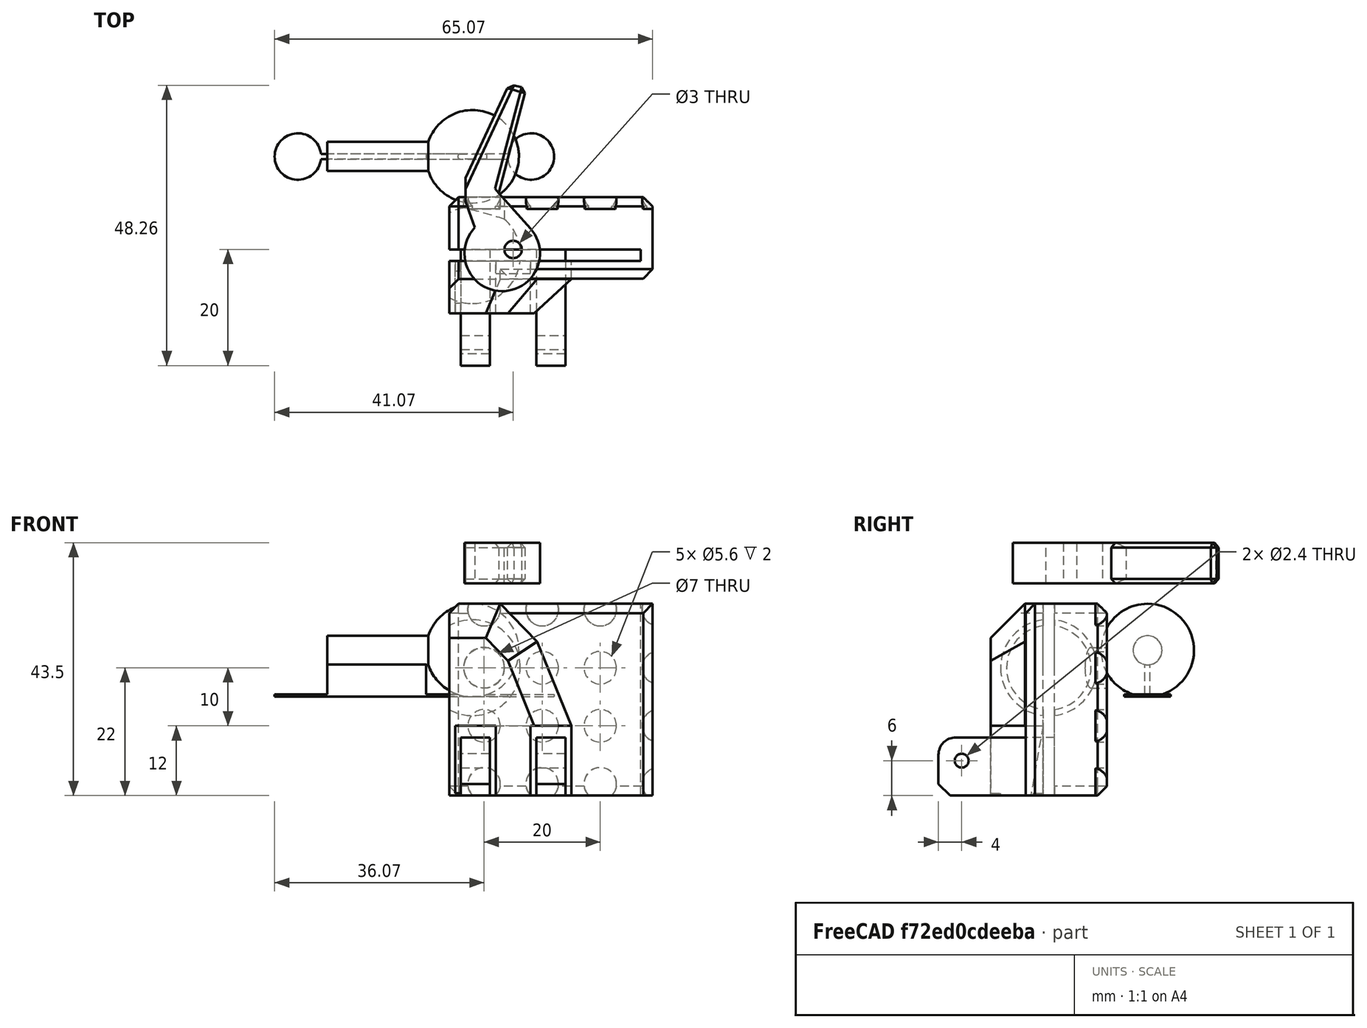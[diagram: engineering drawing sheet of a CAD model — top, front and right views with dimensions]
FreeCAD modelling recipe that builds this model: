
FCSTD DOCUMENT  (FreeCAD 0.18R4 (GitTag))
Label: Ballsocket
License: All rights reserved
LicenseURL: http://en.wikipedia.org/wiki/All_rights_reserved
objects: Sketcher::SketchObject×15, PartDesign::Pocket×7, PartDesign::Pad×4, PartDesign::Chamfer×4, Part::FeaturePython×4, Mesh::Feature×3, Part::Sphere×2, PartDesign::Body×2, Part::MultiFuse×2, PartDesign::Fillet×1, Part::Cylinder×1, Part::Box×1, PartDesign::LinearPattern×1, Part::Extrusion×1, Part::Cut×1, App::DocumentObjectGroup×1
note: 57 computed .brp shape members not serialized (recipe doc carries the construction recipe); baked Part::Feature solids carry a one-line shape summary decoded from their .brp

FEATURE [Sketcher::SketchObject] Sketch
  MapMode = 5
  Support = -> [XY_Plane]
  sketch-geometry (4):
    g0: LineSegment StartX=-22 StartY=18 StartZ=0 EndX=13 EndY=18 EndZ=0
    g1: LineSegment StartX=13 StartY=18 StartZ=0 EndX=13 EndY=-15 EndZ=0
    g2: LineSegment StartX=13 StartY=-15 StartZ=0 EndX=-22 EndY=-15 EndZ=0
    g3: LineSegment StartX=-22 StartY=-15 StartZ=0 EndX=-22 EndY=18 EndZ=0
  constraints (12):
    c: Coincident(g0,g1)
    c: Coincident(g1,g2)
    c: Coincident(g2,g3)
    c: Coincident(g3,g0)
    c: Horizontal(g2)
    c: Vertical(g1)
    c: DistanceX(g2) = -22
    c: DistanceY(g2) = -15
    c: Horizontal(g0)
    c: DistanceX(g0) = 13
    c: Vertical(g3)
    c: DistanceY(g0) = 18
FEATURE [PartDesign::Pad] Pad
  Length = 20
  Length2 = 100
  Profile = -> Sketch
  Refine = true
  Type = 0
FEATURE [Sketcher::SketchObject] Sketch001
  MapMode = 5
  Placement = pos=(0,0,20) rot=(0,0,1;0rad)
  Support = -> [Pad]
  sketch-geometry (8):
    g0: LineSegment StartX=-21 StartY=-3 StartZ=0 EndX=-14 EndY=-3 EndZ=0
    g1: LineSegment StartX=-14 StartY=-3 StartZ=0 EndX=-14 EndY=-15 EndZ=0
    g2: LineSegment StartX=-14 StartY=-15 StartZ=0 EndX=-21 EndY=-15 EndZ=0
    g3: LineSegment StartX=-21 StartY=-15 StartZ=0 EndX=-21 EndY=-3 EndZ=0
    g4: LineSegment StartX=-8 StartY=-3 StartZ=0 EndX=-1 EndY=-3 EndZ=0
    g5: LineSegment StartX=-1 StartY=-3 StartZ=0 EndX=-1 EndY=-15 EndZ=0
    g6: LineSegment StartX=-1 StartY=-15 StartZ=0 EndX=-8 EndY=-15 EndZ=0
    g7: LineSegment StartX=-8 StartY=-15 StartZ=0 EndX=-8 EndY=-3 EndZ=0
  constraints (24):
    c: Coincident(g0,g1)
    c: Coincident(g1,g2)
    c: Coincident(g2,g3)
    c: Coincident(g3,g0)
    c: Horizontal(g0)
    c: Horizontal(g2)
    c: Vertical(g1)
    c: Coincident(g4,g5)
    c: Coincident(g5,g6)
    c: Coincident(g6,g7)
    c: Coincident(g7,g4)
    c: Horizontal(g4)
    c: Horizontal(g6)
    c: Vertical(g5)
    c: Equal(g7,g3)
    c: DistanceX(g0) = -21
    c: DistanceX(g0,g0) = 7
    c: DistanceX(g0,g4) = 6
    c: Distance(g1) = 12
    c: Horizontal(g0,g4)
    c: Vertical(g3)
    c: Vertical(g7)
    c: DistanceY(g2) = -15
    c: DistanceX(g4,g4) = 7
FEATURE [PartDesign::Pocket] Pocket
  BaseFeature = -> Pad
  Length = 10
  Length2 = 100
  Profile = -> Sketch001
  Refine = true
  Type = 0
FEATURE [Sketcher::SketchObject] Sketch003
  MapMode = 5
  Placement = pos=(0,0,0) rot=(0.57735,0.57735,0.57735;2.0944rad)
  Support = -> [YZ_Plane]
  sketch-geometry (1):
    g0: Circle CenterX=-9 CenterY=25 CenterZ=0 NormalX=0 NormalY=0 NormalZ=1 AngleXU=0 Radius=1.2
  constraints (3):
    c: DistanceY(g0) = 25
    c: Radius(g0) = 1.2
    c: DistanceX(g0) = -9
FEATURE [Sketcher::SketchObject] Sketch004
  MapMode = 5
  Placement = pos=(0,0,0) rot=(1,0,0;1.5708rad)
  Support = -> [XZ_Plane]
  sketch-geometry (4):
    g0: LineSegment StartX=-25 StartY=11 StartZ=0 EndX=11 EndY=11 EndZ=0
    g1: LineSegment StartX=11 StartY=11 StartZ=0 EndX=11 EndY=9 EndZ=0
    g2: LineSegment StartX=11 StartY=9 StartZ=0 EndX=-25 EndY=9 EndZ=0
    g3: LineSegment StartX=-25 StartY=9 StartZ=0 EndX=-25 EndY=11 EndZ=0
  constraints (12):
    c: Coincident(g0,g1)
    c: Coincident(g1,g2)
    c: Coincident(g2,g3)
    c: Coincident(g3,g0)
    c: Horizontal(g0)
    c: Horizontal(g2)
    c: Vertical(g1)
    c: Vertical(g3)
    c: DistanceX(g0) = 11
    c: DistanceX(g0) = -25
    c: DistanceY(g2) = 9
    c: DistanceY(g0) = 11
FEATURE [PartDesign::Pocket] Pocket002
  BaseFeature = -> Pocket
  Length = 5
  Length2 = 100
  Midplane = true
  Profile = -> Sketch004
  Refine = true
  Type = 1
FEATURE [Sketcher::SketchObject] Sketch002
  MapMode = 5
  Placement = pos=(0,-2e-15,9) rot=(0,0,1;0rad)
  Support = -> [Pocket002]
  sketch-geometry (8):
    g0: LineSegment StartX=-20 StartY=-5 StartZ=0 EndX=-15 EndY=-5 EndZ=0
    g1: LineSegment StartX=-15 StartY=-5 StartZ=0 EndX=-15 EndY=-15 EndZ=0
    g2: LineSegment StartX=-15 StartY=-15 StartZ=0 EndX=-20 EndY=-15 EndZ=0
    g3: LineSegment StartX=-20 StartY=-15 StartZ=0 EndX=-20 EndY=-5 EndZ=0
    g4: LineSegment StartX=-7 StartY=-5 StartZ=0 EndX=-2 EndY=-5 EndZ=0
    g5: LineSegment StartX=-2 StartY=-5 StartZ=0 EndX=-2 EndY=-15 EndZ=0
    g6: LineSegment StartX=-2 StartY=-15 StartZ=0 EndX=-7 EndY=-15 EndZ=0
    g7: LineSegment StartX=-7 StartY=-15 StartZ=0 EndX=-7 EndY=-5 EndZ=0
  constraints (24):
    c: Coincident(g0,g1)
    c: Coincident(g1,g2)
    c: Coincident(g2,g3)
    c: Coincident(g3,g0)
    c: Horizontal(g0)
    c: Horizontal(g2)
    c: Vertical(g1)
    c: Coincident(g4,g5)
    c: Coincident(g5,g6)
    c: Coincident(g6,g7)
    c: Coincident(g7,g4)
    c: Horizontal(g4)
    c: Horizontal(g6)
    c: Vertical(g5)
    c: DistanceX(g0) = -20
    c: DistanceX(g0,g0) = 5
    c: DistanceX(g0,g4) = 8
    c: Equal(g0,g4)
    c: Equal(g7,g3)
    c: Distance(g3) = 10
    c: Vertical(g3)
    c: Vertical(g7)
    c: Horizontal(g4,g0)
    c: DistanceY(g2) = -15
FEATURE [PartDesign::Pad] Pad001
  BaseFeature = -> Pocket002
  Length = 20
  Length2 = 100
  Profile = -> Sketch002
  Refine = true
  Type = 0
FEATURE [PartDesign::Pocket] Pocket001
  BaseFeature = -> Pad001
  Length = 5
  Length2 = 100
  Profile = -> Sketch003
  Refine = true
  Type = 1
FEATURE [Part::Sphere] Sphere
  Angle1 = -90
  Angle2 = 90
  Angle3 = 360
  AttacherType = Attacher::AttachEngine3D
  Placement = pos=(-18,7,10) rot=(0,0,1;0rad)
  Radius = 8.3
FEATURE [Sketcher::SketchObject] Sketch005
  MapMode = 5
  Placement = pos=(0,0,20) rot=(0,0,1;0rad)
  Support = -> [Pocket001]
  sketch-geometry (7):
    g0: LineSegment StartX=-6.87841 StartY=11.5067 StartZ=0 EndX=-1 EndY=-3 EndZ=0
    g1: LineSegment StartX=-1 StartY=-3 StartZ=0 EndX=-1 EndY=-16.5217 EndZ=0
    g2: LineSegment StartX=-1 StartY=-16.5217 StartZ=0 EndX=16.1456 EndY=-16.5217 EndZ=0
    g3: LineSegment StartX=16.1456 StartY=-16.5217 StartZ=0 EndX=16.1456 EndY=20.3335 EndZ=0
    g4: LineSegment StartX=-13.2042 StartY=18 StartZ=0 EndX=-18.5565 EndY=20.3335 EndZ=0
    g5: LineSegment StartX=-18.5565 StartY=20.3335 StartZ=0 EndX=16.1456 EndY=20.3335 EndZ=0
    g6: LineSegment StartX=-13.2042 StartY=18 StartZ=0 EndX=-6.87841 EndY=11.5067 EndZ=0
  constraints (17):
    c: Vertical(g1)
    c: Coincident(g1,g2)
    c: Horizontal(g2)
    c: Coincident(g2,g3)
    c: Vertical(g3)
    c: Coincident(g5,g4)
    c: Coincident(g5,g3)
    c: Horizontal(g5)
    c: Coincident(g0,g1)
    c: DistanceX(g0) = -1
    c: DistanceY(g0) = -3
    c: DistanceX(g0) = -6.87841
    c: DistanceY(g0) = 11.5067
    c: DistanceX(g4) = -13.2042
    c: DistanceY(g4) = 18
    c: Coincident(g6,g4)
    c: Coincident(g6,g0)
FEATURE [PartDesign::Pocket] Pocket003
  BaseFeature = -> Pocket001
  Length = 6
  Length2 = 100
  Profile = -> Sketch005
  Refine = true
  Type = 0
FEATURE [PartDesign::Chamfer] Chamfer
  Base = -> Pocket003 [Edge5,Edge21,Edge29]
  BaseFeature = -> Pocket003
  Size = 5.9
FEATURE [Sketcher::SketchObject] Sketch006
  ExternalGeometry = -> [Chamfer]
  MapMode = 5
  Placement = pos=(0,0,20) rot=(0,0,1;0rad)
  Support = -> [Chamfer]
FEATURE [PartDesign::Chamfer] Chamfer001
  Base = -> Chamfer [Face8,Edge9,Edge41,Edge4,Edge24,Edge17,Edge3]
  BaseFeature = -> Chamfer
  Size = 1.6
FEATURE [PartDesign::Chamfer] Chamfer002
  Base = -> Chamfer001 [Edge78,Edge83]
  BaseFeature = -> Chamfer001
  Size = 2
FEATURE [PartDesign::Fillet] Fillet
  Base = -> Chamfer002 [Edge87,Edge75]
  BaseFeature = -> Chamfer002
  Radius = 3
FEATURE [Sketcher::SketchObject] Sketch007
  MapMode = 5
  Placement = pos=(0,0,0) rot=(0.57735,0.57735,0.57735;2.0944rad)
  Support = -> [YZ_Plane001]
  sketch-geometry (11):
    g0: ArcOfCircle CenterX=-0.68404 CenterY=-1.87939 CenterZ=0 NormalX=0 NormalY=0 NormalZ=1 AngleXU=0 Radius=6.5 StartAngle=0.843713 EndAngle=5.47308
    g1: LineSegment [constr] StartX=0 StartY=0 StartZ=0 EndX=-0.68404 EndY=-1.87939 EndZ=0
    g2: LineSegment StartX=3.79722 StartY=-6.58771 StartZ=0 EndX=8.22696 EndY=-8.2 EndZ=0
    g3: LineSegment StartX=8.22696 StartY=-8.2 StartZ=0 EndX=12.3057 EndY=-8.2 EndZ=0
    g4: LineSegment StartX=12.3057 StartY=-8.2 StartZ=0 EndX=28.4613 EndY=-0.655032 EndZ=0
    g5: LineSegment StartX=3.63647 StartY=2.97687 StartZ=0 EndX=9.73628 EndY=-2.45001 EndZ=0
    g6: LineSegment StartX=9.73628 StartY=-2.45001 StartZ=0 EndX=27.7024 EndY=2.2474 EndZ=0
    g7: LineSegment StartX=27.7024 StartY=2.2474 StartZ=0 EndX=28.4613 EndY=-0.655032 EndZ=0
    g8: Circle CenterX=0 CenterY=0 CenterZ=0 NormalX=0 NormalY=0 NormalZ=1 AngleXU=0 Radius=1.5
    g9: LineSegment [constr] StartX=3.08498 StartY=3.46752 StartZ=0 EndX=0.99704 EndY=1.12067 EndZ=0
    g10: LineSegment [constr] StartX=-0.68404 StartY=-8.37939 StartZ=0 EndX=-0.68404 EndY=-12.1798 EndZ=0
  constraints (28):
    c: Coincident(g1,g-1)
    c: Coincident(g1,g0)
    c: Distance(g1) = 2
    c: Radius(g0) = 6.5
    c: Coincident(g2,g0)
    c: Perpendicular(g1,g2)
    c: Coincident(g2,g3)
    c: Horizontal(g3)
    c: Coincident(g3,g4)
    c: Tangent(g0,g5) = 1.5708
    c: Coincident(g6,g5)
    c: Coincident(g7,g6)
    c: Coincident(g7,g4)
    c: Perpendicular(g7,g6)
    c: Distance(g7) = 3
    c: Coincident(g8,g-1)
    c: Radius(g8) = 1.5
    c: PointOnObject(g9,g5)
    c: PointOnObject(g9,g8)
    c: Distance(g9) = 3.1412
    c: Perpendicular(g5,g9)
    c: Perpendicular(g8,g9)
    c: Angle(g1) = -1.91986
    c: DistanceY(g2) = -8.2
    c: PointOnObject(g10,g0)
    c: Vertical(g10)
    c: Perpendicular(g0,g10)
    c: DistanceY(g10) = -8.37939
FEATURE [PartDesign::Pad] Pad002
  Length = 7
  Length2 = 100
  Midplane = true
  Placement = pos=(0,0,0) rot=(0.57735,0.57735,0.57735;2.0944rad)
  Profile = -> Sketch007
  Refine = true
  Type = 0
FEATURE [PartDesign::Chamfer] Chamfer003
  Base = -> Pad002 [Edge18,Edge12,Edge19,Edge13,Face5]
  BaseFeature = -> Pad002
  Placement = pos=(0,0,0) rot=(0.57735,0.57735,0.57735;2.0944rad)
  Size = 0.8
FEATURE [PartDesign::Body] Body001  label="Lever"
  Group = -> [Sketch007,Pad002,Chamfer003]
  Origin = -> Origin001
  Placement = pos=(-11,-9,25) rot=(0,0,1;0rad)
  Tip = -> Chamfer003
FEATURE [Part::Sphere] Sphere001
  Angle1 = -90
  Angle2 = 90
  Angle3 = 360
  AttacherType = Attacher::AttachEngine3D
  Placement = pos=(-18,7,10) rot=(0,0,1;0rad)
  Radius = 8
FEATURE [Part::Cylinder] Cylinder
  Angle = 360
  AttacherType = Attacher::AttachEngine3D
  Height = 25
  Placement = pos=(-18,7,10) rot=(0,-1,0;1.5708rad)
  Radius = 2.5
FEATURE [Part::Box] Box  label="Cube"
  AttacherType = Attacher::AttachEngine3D
  Height = 8
  Length = 17
  Placement = pos=(-43,6.55,2) rot=(0,0,1;0rad)
  Width = 0.9
FEATURE [Part::MultiFuse] Fusion  label="Ball_withoutsupport"
  Refine = true
  Shapes = -> [Sphere001,Cylinder,Box]
FEATURE [Sketcher::SketchObject] Sketch008
  MapMode = 5
  Placement = pos=(0,0,20) rot=(0,0,1;0rad)
  Support = -> [Pad]
  sketch-geometry (2):
    g0: Circle CenterX=4 CenterY=7 CenterZ=0 NormalX=0 NormalY=0 NormalZ=1 AngleXU=0 Radius=3.3
    g1: Circle [constr] CenterX=4 CenterY=7 CenterZ=0 NormalX=0 NormalY=0 NormalZ=1 AngleXU=0 Radius=6.5
  constraints (5):
    c: DistanceY(g0) = 7
    c: Radius(g0) = 3.3
    c: Coincident(g1,g0)
    c: Radius(g1) = 6.5
    c: DistanceX(g0) = 4
FEATURE [Sketcher::SketchObject] Sketch009
  MapMode = 5
  Placement = pos=(0,0,14) rot=(0,0,1;0rad)
  Support = -> [Pocket003]
  expr: Constraints[4] = Sketch008.Constraints[4]
  expr: Constraints[3] = Sketch008.Constraints[3]
  expr: Constraints[1] = Sketch008.Constraints[1]
  expr: Constraints[0] = Sketch008.Constraints[0]
  sketch-geometry (2):
    g0: Circle [constr] CenterX=4 CenterY=7 CenterZ=0 NormalX=0 NormalY=0 NormalZ=1 AngleXU=0 Radius=3.3
    g1: Circle CenterX=4 CenterY=7 CenterZ=0 NormalX=0 NormalY=0 NormalZ=1 AngleXU=0 Radius=6.5
  constraints (5):
    c: DistanceY(g0) = 7
    c: Radius(g0) = 3.3
    c: Coincident(g1,g0)
    c: Radius(g1) = 6.5
    c: DistanceX(g0) = 4
FEATURE [Sketcher::SketchObject] Sketch010
  MapMode = 5
  Support = -> [XY_Plane]
  expr: Constraints[4] = Sketch008.Constraints[4]
  expr: Constraints[3] = Sketch008.Constraints[3]
  expr: Constraints[1] = Sketch008.Constraints[1]
  expr: Constraints[0] = Sketch008.Constraints[0]
  sketch-geometry (11):
    g0: Circle [constr] CenterX=4 CenterY=7 CenterZ=0 NormalX=0 NormalY=0 NormalZ=1 AngleXU=0 Radius=3.3
    g1: Circle [constr] CenterX=4 CenterY=7 CenterZ=0 NormalX=0 NormalY=0 NormalZ=1 AngleXU=0 Radius=6.5
    g2: Circle CenterX=14 CenterY=-13 CenterZ=0 NormalX=0 NormalY=0 NormalZ=1 AngleXU=0 Radius=2.8
    g3: Circle CenterX=4 CenterY=-13 CenterZ=0 NormalX=0 NormalY=0 NormalZ=1 AngleXU=0 Radius=2.8
    g4: Circle CenterX=-6 CenterY=-13 CenterZ=0 NormalX=0 NormalY=0 NormalZ=1 AngleXU=0 Radius=2.8
    g5: Circle CenterX=-16 CenterY=-13 CenterZ=0 NormalX=0 NormalY=0 NormalZ=1 AngleXU=0 Radius=2.8
    g6: Circle [constr] CenterX=-26 CenterY=-13 CenterZ=0 NormalX=0 NormalY=0 NormalZ=1 AngleXU=0 Radius=2.8
    g7: LineSegment [constr] StartX=14 StartY=-13 StartZ=0 EndX=4 EndY=-13 EndZ=0
    g8: LineSegment [constr] StartX=-6 StartY=-13 StartZ=0 EndX=4 EndY=-13 EndZ=0
    g9: LineSegment [constr] StartX=-6 StartY=-13 StartZ=0 EndX=-16 EndY=-13 EndZ=0
    g10: LineSegment [constr] StartX=-16 StartY=-13 StartZ=0 EndX=-26 EndY=-13 EndZ=0
  constraints (28):
    c: DistanceY(g0) = 7
    c: Radius(g0) = 3.3
    c: Coincident(g1,g0)
    c: Radius(g1) = 6.5
    c: DistanceX(g0) = 4
    c: DistanceY(g2,g0) = 20
    c: Coincident(g7,g2)
    c: Coincident(g7,g3)
    c: Coincident(g8,g4)
    c: Coincident(g8,g3)
    c: Coincident(g9,g4)
    c: Coincident(g9,g5)
    c: Horizontal(g9)
    c: Coincident(g10,g5)
    c: Coincident(g10,g6)
    c: Horizontal(g10)
    c: Horizontal(g8)
    c: Horizontal(g7)
    c: Equal(g7,g8)
    c: Equal(g8,g9)
    c: Equal(g9,g10)
    c: Vertical(g3,g0)
    c: Distance(g7) = 10
    c: Equal(g2,g3)
    c: Equal(g3,g4)
    c: Equal(g4,g5)
    c: Equal(g5,g6)
    c: Radius(g3) = 2.8
FEATURE [PartDesign::Pocket] Pocket006
  BaseFeature = -> Fillet
  Length = 2
  Length2 = 100
  Profile = -> Sketch010
  Refine = true
  Reversed = true
  Type = 0
FEATURE [PartDesign::LinearPattern] LinearPattern
  BaseFeature = -> Pocket006
  Direction = -> Sketch010 [V_Axis]
  Length = 30
  Occurrences = 4
  Originals = -> [Pocket006]
  Refine = true
FEATURE [Sketcher::SketchObject] Sketch011
  MapMode = 5
  Placement = pos=(0,0,2) rot=(1,0,0;3.14159rad)
  Support = -> [Fusion]
  sketch-geometry (6):
    g0: LineSegment StartX=-44.0943 StartY=-6.55 StartZ=0 EndX=-11.9024 EndY=-6.55 EndZ=0
    g1: LineSegment [constr] StartX=-11.9024 StartY=-6.55 StartZ=0 EndX=-11.9024 EndY=-7.45 EndZ=0
    g2: LineSegment StartX=-11.9024 StartY=-7.45 StartZ=0 EndX=-44.0943 EndY=-7.45 EndZ=0
    g3: LineSegment [constr] StartX=-44.0943 StartY=-7.45 StartZ=0 EndX=-44.0943 EndY=-6.55 EndZ=0
    g4: ArcOfCircle CenterX=-7.92778 CenterY=-7 CenterZ=0 NormalX=0 NormalY=0 NormalZ=1 AngleXU=0 Radius=4 StartAngle=3.25433 EndAngle=9.31204
    g5: ArcOfCircle CenterX=-48.0689 CenterY=-7 CenterZ=0 NormalX=0 NormalY=0 NormalZ=1 AngleXU=0 Radius=4 StartAngle=0.112739 EndAngle=6.17045
  constraints (16):
    c: Coincident(g0,g1)
    c: Coincident(g1,g2)
    c: Coincident(g2,g3)
    c: Coincident(g3,g0)
    c: Horizontal(g0)
    c: Horizontal(g2)
    c: Vertical(g1)
    c: Vertical(g3)
    c: Distance(g3) = 0.9
    c: DistanceY(g0) = -6.55
    c: Coincident(g4,g0)
    c: Coincident(g4,g2)
    c: Radius(g4) = 4
    c: Coincident(g5,g0)
    c: Coincident(g5,g2)
    c: Radius(g5) = 4
FEATURE [Part::Extrusion] Extrude
  Base = -> Sketch011
  Dir = (0,0,-1)
  DirMode = 2
  FaceMakerClass = Part::FaceMakerBullseye
  LengthFwd = 0.4
  LengthRev = 0
  Reversed = true
  Solid = true
  Symmetric = false
FEATURE [Part::MultiFuse] Fusion001  label="Ball"
  Refine = true
  Shapes = -> [Fusion,Extrude]
FEATURE [Sketcher::SketchObject] Sketch012
  MapMode = 5
  Placement = pos=(0,0,0) rot=(1,0,0;3.14159rad)
  Support = -> [Pad]
  sketch-geometry (1):
    g0: Circle CenterX=-16 CenterY=-7 CenterZ=0 NormalX=0 NormalY=0 NormalZ=1 AngleXU=0 Radius=3.5
  constraints (3):
    c: DistanceX(g0) = -16
    c: DistanceY(g0) = -7
    c: Radius(g0) = 3.5
FEATURE [PartDesign::Pocket] Pocket007
  BaseFeature = -> LinearPattern
  Length = 8
  Length2 = 100
  Profile = -> Sketch012
  Refine = true
  Type = 0
FEATURE [Sketcher::SketchObject] Sketch013
  MapMode = 5
  Placement = pos=(0,-15,0) rot=(1,0,0;1.5708rad)
  Support = -> [Pad]
  sketch-geometry (8):
    g0: LineSegment StartX=-21.5877 StartY=20 StartZ=0 EndX=-18.0644 EndY=20 EndZ=0
    g1: LineSegment StartX=-18.0644 StartY=20 StartZ=0 EndX=-18.0644 EndY=18.3 EndZ=0
    g2: LineSegment StartX=-18.0644 StartY=18.3 StartZ=0 EndX=-21.5877 EndY=18.3 EndZ=0
    g3: LineSegment StartX=-21.5877 StartY=18.3 StartZ=0 EndX=-21.5877 EndY=20 EndZ=0
    g4: LineSegment StartX=-21.4003 StartY=12.7 StartZ=0 EndX=-17.5021 EndY=12.7 EndZ=0
    g5: LineSegment StartX=-17.5021 StartY=12.7 StartZ=0 EndX=-17.5021 EndY=11 EndZ=0
    g6: LineSegment StartX=-17.5021 StartY=11 StartZ=0 EndX=-21.4003 EndY=11 EndZ=0
    g7: LineSegment StartX=-21.4003 StartY=11 StartZ=0 EndX=-21.4003 EndY=12.7 EndZ=0
  constraints (20):
    c: Coincident(g0,g1)
    c: Coincident(g1,g2)
    c: Coincident(g2,g3)
    c: Coincident(g3,g0)
    c: Horizontal(g0)
    c: Horizontal(g2)
    c: Vertical(g1)
    c: Vertical(g3)
    c: DistanceY(g0) = 20
    c: Distance(g3) = 1.7
    c: Coincident(g4,g5)
    c: Coincident(g5,g6)
    c: Coincident(g6,g7)
    c: Coincident(g7,g4)
    c: Horizontal(g4)
    c: Horizontal(g6)
    c: Vertical(g5)
    c: Vertical(g7)
    c: DistanceY(g6) = 11
    c: Equal(g7,g3)
FEATURE [PartDesign::Pad] Pad003
  BaseFeature = -> Pocket007
  Length = 0.4
  Length2 = 100
  Profile = -> Sketch013
  Refine = true
  Reversed = true
  Type = 0
FEATURE [Sketcher::SketchObject] Sketch014
  MapMode = 5
  Placement = pos=(-14,0,0) rot=(0.57735,-0.57735,-0.57735;2.0944rad)
  Support = -> [Pocket]
  sketch-geometry (3):
    g0: LineSegment StartX=3 StartY=11 StartZ=0 EndX=23 EndY=14.5265 EndZ=0
    g1: LineSegment StartX=3 StartY=11 StartZ=0 EndX=23 EndY=11 EndZ=0
    g2: LineSegment StartX=23 StartY=11 StartZ=0 EndX=23 EndY=14.5265 EndZ=0
  constraints (9):
    c: DistanceX(g0) = 3
    c: DistanceY(g0) = 11
    c: Angle(g0) = 0.174533
    c: Coincident(g0,g1)
    c: Horizontal(g1)
    c: Coincident(g1,g2)
    c: Vertical(g2)
    c: DistanceX(g1,g1) = 20
    c: Coincident(g0,g2)
FEATURE [PartDesign::Pocket] Pocket008
  BaseFeature = -> Pad003
  Length = 6
  Length2 = 100
  Profile = -> Sketch014
  Refine = true
  Type = 0
FEATURE [PartDesign::Body] Body  label="Socketbody"
  Group = -> [Sketch,Pad,Sketch001,Pocket,Pocket002,Sketch002,Pad001,Sketch003,Pocket001,Sketch004,Sketch005,Pocket003,Chamfer,Sketch006,Chamfer001,Chamfer002,Fillet,Pocket006,LinearPattern,Pocket007,Sketch012,Sketch008,Sketch009,Sketch010,Sketch013,Pad003,Sketch014,Pocket008]
  Origin = -> Origin
  Tip = -> Pocket008
FEATURE [Part::FeaturePython] Clone  label="Socketbody001"  # Draft clone (typed FeaturePython)
  AttacherType = Attacher::AttachEngine3D
  Fuse = false
  Objects = -> [Body]
  Scale = (1,1,1)
FEATURE [Part::Cut] Cut  label="Socket"
  Base = -> Clone
  Refine = true
  Tool = -> Sphere
FEATURE [Part::FeaturePython] Clone001  label="out_Socket"  # Draft clone (typed FeaturePython)
  AttacherType = Attacher::AttachEngine3D
  Fuse = false
  Objects = -> [Cut]
  Placement = pos=(0,0,0) rot=(1,0,0;1.5708rad)
  Scale = (1,1,1)
FEATURE [Part::FeaturePython] Clone002  label="out_Ball"  # Draft clone (typed FeaturePython)
  AttacherType = Attacher::AttachEngine3D
  Fuse = false
  Objects = -> [Fusion001]
  Scale = (1,1,1)
FEATURE [Part::FeaturePython] Clone003  label="out_Lever"  # Draft clone (typed FeaturePython)
  AttacherType = Attacher::AttachEngine3D
  Fuse = false
  Objects = -> [Body001]
  Placement = pos=(-11,-9,25) rot=(0,1,0;1.5708rad)
  Scale = (1,1,1)
FEATURE [App::DocumentObjectGroup] Group  label="Oriented for printing"
  Group = -> [Clone001,Clone002,Clone003]
FEATURE [Mesh::Feature] Mesh  label="out_Socket (Meshed)"
FEATURE [Mesh::Feature] Mesh001  label="out_Ball (Meshed)"
FEATURE [Mesh::Feature] Mesh002  label="out_Lever (Meshed)"
